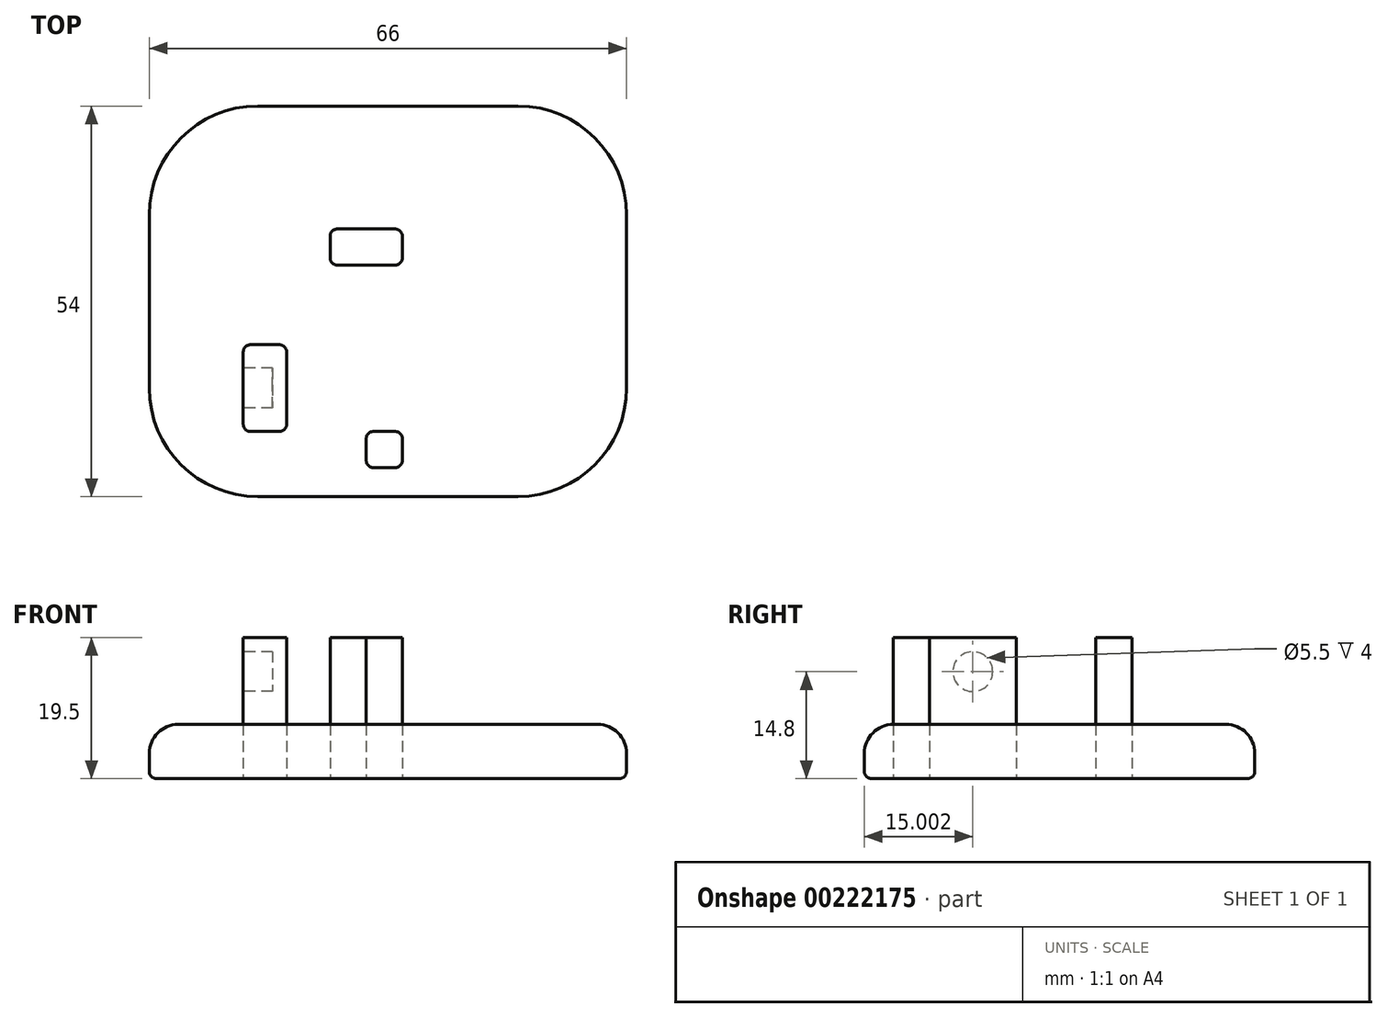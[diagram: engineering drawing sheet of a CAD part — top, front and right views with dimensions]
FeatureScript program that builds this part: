
annotation { "Feature Type Name" : "Feature", "Feature Type Description" : "" }
export const myFeature = defineFeature(function(context is Context, id is Id, definition is map)
    precondition{}
    {
        {
            var Q0;
            Q0=qCreatedBy(makeId("Top.planeOp"),FACE);
            var sketch = newSketch(context, id + "F0", { "sketchPlane" : qUnion([Q0])});
            skLineSegment(sketch, "E0.bottom", {"start": v(-30.44, 33.23) * mm, "end": v(35.56, 33.23) * mm});
            skLineSegment(sketch, "E0.top", {"start": v(-30.44, -20.77) * mm, "end": v(35.56, -20.77) * mm});
            skLineSegment(sketch, "E0.left", {"start": v(-30.44, 33.23) * mm, "end": v(-30.44, -20.77) * mm});
            skLineSegment(sketch, "E0.right", {"start": v(35.56, 33.23) * mm, "end": v(35.56, -20.77) * mm});
            skSolve(sketch);
        }
        {
            var Q0;
            Q0=makeQuery(id+"F0.imprint","IMPRINT",FACE,{"disambiguationData":[TD([[makeQuery(id+"F0.imprint","IMPRINT",EDGE,{"derivedFrom":sQuery(id+"F0.wireOp",EDGE,"E0.bottom")}),-1.0]])]});
            extrude(context, id + "F1", {"entities" : qUnion([Q0]), "depth" : 7.5 * mm});
        }
        {
            var Q0;
            Q0=makeQuery(id+"F1.opExtrude","CAP_FACE",FACE,{"disambiguationData":[OSD([sQuery(id+"F0.wireOp",EDGE,"E0.bottom"),sQuery(id+"F0.wireOp",EDGE,"E0.top"),sQuery(id+"F0.wireOp",EDGE,"E0.left"),sQuery(id+"F0.wireOp",EDGE,"E0.right")])],"isStart":false});
            fillet(context, id + "F2", {"entities" : qUnion([Q0]), "radius" : 4 * mm, "tangentPropagation" : true, "allowEdgeOverflow" : false});
        }
        {
            var Q0;
            Q0=makeQuery(id+"F1.opExtrude","CAP_FACE",FACE,{"disambiguationData":[OSD([sQuery(id+"F0.wireOp",EDGE,"E0.bottom"),sQuery(id+"F0.wireOp",EDGE,"E0.top"),sQuery(id+"F0.wireOp",EDGE,"E0.left"),sQuery(id+"F0.wireOp",EDGE,"E0.right")])],"isStart":true});
            fillet(context, id + "F3", {"entities" : qUnion([Q0]), "radius" : 1 * mm, "tangentPropagation" : true, "allowEdgeOverflow" : false});
        }
        {
            var Q0;
            Q0=qCreatedBy(makeId("Top.planeOp"),FACE);
            var sketch = newSketch(context, id + "F4", { "sketchPlane" : qUnion([Q0])});
            skLineSegment(sketch, "E1.bottom", {"start": v(-17.44, 0.23) * mm, "end": v(-11.44, 0.23) * mm});
            skLineSegment(sketch, "E1.top", {"start": v(-17.44, -11.77) * mm, "end": v(-11.44, -11.77) * mm});
            skLineSegment(sketch, "E1.left", {"start": v(-17.44, 0.23) * mm, "end": v(-17.44, -11.77) * mm});
            skLineSegment(sketch, "E1.right", {"start": v(-11.44, 0.23) * mm, "end": v(-11.44, -11.77) * mm});
            skLineSegment(sketch, "E2.bottom", {"start": v(-5.44, 16.23) * mm, "end": v(4.56, 16.23) * mm});
            skLineSegment(sketch, "E2.top", {"start": v(-5.44, 11.23) * mm, "end": v(4.56, 11.23) * mm});
            skLineSegment(sketch, "E2.left", {"start": v(-5.44, 16.23) * mm, "end": v(-5.44, 11.23) * mm});
            skLineSegment(sketch, "E2.right", {"start": v(4.56, 16.23) * mm, "end": v(4.56, 11.23) * mm});
            skLineSegment(sketch, "E3.bottom", {"start": v(-0.44, -11.77) * mm, "end": v(4.56, -11.77) * mm});
            skLineSegment(sketch, "E3.top", {"start": v(-0.44, -16.77) * mm, "end": v(4.56, -16.77) * mm});
            skLineSegment(sketch, "E3.left", {"start": v(-0.44, -11.77) * mm, "end": v(-0.44, -16.77) * mm});
            skLineSegment(sketch, "E3.right", {"start": v(4.56, -11.77) * mm, "end": v(4.56, -16.77) * mm});
            skLineSegment(sketch, "E4", {"start": v(-17.44, -11.77) * mm, "end": v(-0.15, -11.77) * mm, "construction": true});
            skLineSegment(sketch, "E5", {"start": v(4.56, 31.2) * mm, "end": v(4.56, -45.77) * mm, "construction": true});
            skSolve(sketch);
        }
        {
            var Q0;
            Q0=qSketchRegion(id+"F4",true);
            extrude(context, id + "F5", {"entities" : qUnion([Q0]), "depth" : 19.5 * mm});
        }
        {
            var Q0;
            Q0=makeQuery(id+"F5.opExtrude","SWEPT_EDGE",EDGE,{"disambiguationData":[OSD([sQuery(id+"F4.wireOp",EDGE,"E1.top"),sQuery(id+"F4.wireOp",EDGE,"E1.left")])]});
            var Q1;
            Q1=makeQuery(id+"F5.opExtrude","SWEPT_EDGE",EDGE,{"disambiguationData":[OSD([sQuery(id+"F4.wireOp",EDGE,"E1.top"),sQuery(id+"F4.wireOp",EDGE,"E1.right")])]});
            var Q2;
            Q2=makeQuery(id+"F5.opExtrude","SWEPT_EDGE",EDGE,{"disambiguationData":[OSD([sQuery(id+"F4.wireOp",EDGE,"E3.top"),sQuery(id+"F4.wireOp",EDGE,"E3.left")])]});
            var Q3;
            Q3=makeQuery(id+"F5.opExtrude","SWEPT_EDGE",EDGE,{"disambiguationData":[OSD([sQuery(id+"F4.wireOp",EDGE,"E3.top"),sQuery(id+"F4.wireOp",EDGE,"E3.right")])]});
            var Q4;
            Q4=makeQuery(id+"F5.opExtrude","SWEPT_EDGE",EDGE,{"disambiguationData":[OSD([sQuery(id+"F4.wireOp",EDGE,"E2.top"),sQuery(id+"F4.wireOp",EDGE,"E2.right")])]});
            var Q5;
            Q5=makeQuery(id+"F5.opExtrude","SWEPT_EDGE",EDGE,{"disambiguationData":[OSD([sQuery(id+"F4.wireOp",EDGE,"E2.top"),sQuery(id+"F4.wireOp",EDGE,"E2.left")])]});
            var Q6;
            Q6=makeQuery(id+"F5.opExtrude","SWEPT_EDGE",EDGE,{"disambiguationData":[OSD([sQuery(id+"F4.wireOp",EDGE,"E3.bottom"),sQuery(id+"F4.wireOp",EDGE,"E3.right")])]});
            var Q7;
            Q7=makeQuery(id+"F5.opExtrude","SWEPT_EDGE",EDGE,{"disambiguationData":[OSD([sQuery(id+"F4.wireOp",EDGE,"E1.bottom"),sQuery(id+"F4.wireOp",EDGE,"E1.right")])]});
            var Q8;
            Q8=makeQuery(id+"F5.opExtrude","SWEPT_EDGE",EDGE,{"disambiguationData":[OSD([sQuery(id+"F4.wireOp",EDGE,"E2.bottom"),sQuery(id+"F4.wireOp",EDGE,"E2.right")])]});
            var Q9;
            Q9=makeQuery(id+"F5.opExtrude","SWEPT_EDGE",EDGE,{"disambiguationData":[OSD([sQuery(id+"F4.wireOp",EDGE,"E2.bottom"),sQuery(id+"F4.wireOp",EDGE,"E2.left")])]});
            var Q10;
            Q10=makeQuery(id+"F5.opExtrude","SWEPT_EDGE",EDGE,{"disambiguationData":[OSD([sQuery(id+"F4.wireOp",EDGE,"E1.bottom"),sQuery(id+"F4.wireOp",EDGE,"E1.left")])]});
            var Q11;
            Q11=makeQuery(id+"F5.opExtrude","SWEPT_EDGE",EDGE,{"disambiguationData":[OSD([sQuery(id+"F4.wireOp",EDGE,"E3.bottom"),sQuery(id+"F4.wireOp",EDGE,"E3.left")])]});
            fillet(context, id + "F6", {"entities" : qUnion([Q0, Q1, Q2, Q3, Q4, Q5, Q6, Q7, Q8, Q9, Q10, Q11]), "radius" : 1 * mm, "tangentPropagation" : true, "allowEdgeOverflow" : false});
        }
        {
            var Q0;
            Q0=makeQuery(id+"F5.opExtrude","SWEPT_FACE",FACE,{"disambiguationData":[OSD([sQuery(id+"F4.wireOp",EDGE,"E1.left")])]});
            var sketch = newSketch(context, id + "F7", { "sketchPlane" : qUnion([Q0])});
            skCircle(sketch, "E6", {"center": v(5.77, 14.8) * mm, "radius": 2.75 * mm});
            skLineSegment(sketch, "E7", {"start": v(5.77, 19.5) * mm, "end": v(5.77, -11.56) * mm, "construction": true});
            skPoint(sketch, "E7.endSnap0", {"position": v(5.77, 0) * mm});
            skSolve(sketch);
        }
        {
            var Q0;
            Q0=makeQuery(id+"F7.imprint","IMPRINT",FACE,{"disambiguationData":[TD([[makeQuery(id+"F7.imprint","IMPRINT",EDGE,{"derivedFrom":sQuery(id+"F7.wireOp",EDGE,"E6")}),1.0]])]});
            extrude(context, id + "F8", {"entities" : qUnion([Q0]), "operationType" : NewBodyOperationType.REMOVE, "oppositeDirection" : true, "depth" : 4 * mm});
        }
        {
            var Q0;
            Q0=makeQuery(id+"F1.opExtrude","SWEPT_EDGE",EDGE,{"disambiguationData":[OSD([sQuery(id+"F0.wireOp",EDGE,"E0.top"),sQuery(id+"F0.wireOp",EDGE,"E0.right")])]});
            var Q1;
            Q1=makeQuery(id+"F1.opExtrude","SWEPT_EDGE",EDGE,{"disambiguationData":[OSD([sQuery(id+"F0.wireOp",EDGE,"E0.bottom"),sQuery(id+"F0.wireOp",EDGE,"E0.right")])]});
            var Q2;
            Q2=makeQuery(id+"F1.opExtrude","SWEPT_EDGE",EDGE,{"disambiguationData":[OSD([sQuery(id+"F0.wireOp",EDGE,"E0.bottom"),sQuery(id+"F0.wireOp",EDGE,"E0.left")])]});
            var Q3;
            Q3=makeQuery(id+"F1.opExtrude","SWEPT_EDGE",EDGE,{"disambiguationData":[OSD([sQuery(id+"F0.wireOp",EDGE,"E0.top"),sQuery(id+"F0.wireOp",EDGE,"E0.left")])]});
            fillet(context, id + "F9", {"entities" : qUnion([Q0, Q1, Q2, Q3]), "radius" : 15 * mm, "tangentPropagation" : true, "allowEdgeOverflow" : false});
        }
    });
